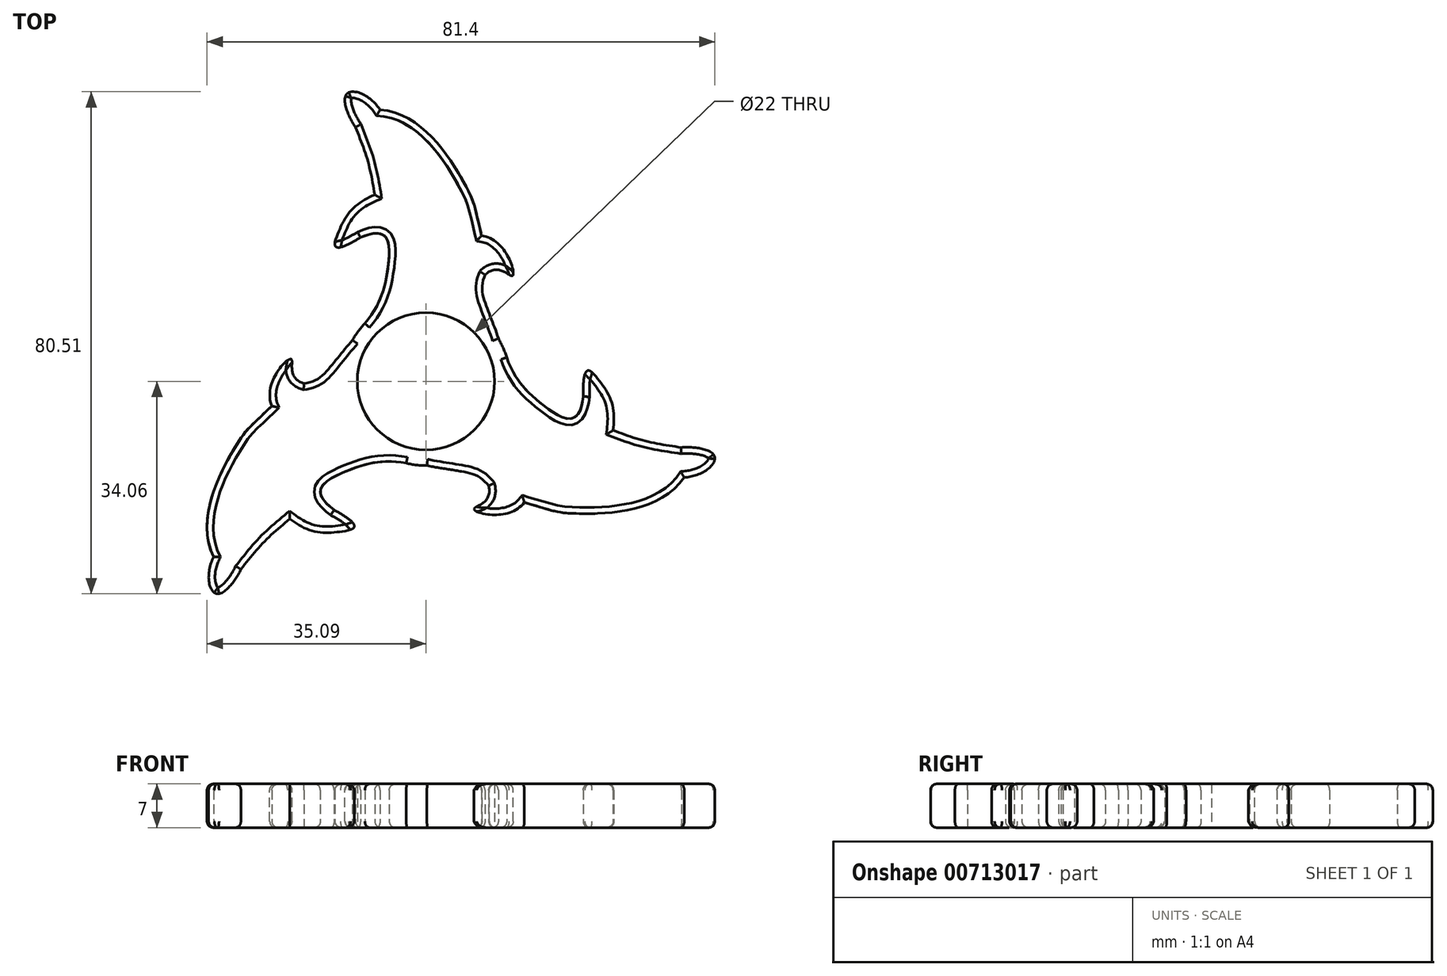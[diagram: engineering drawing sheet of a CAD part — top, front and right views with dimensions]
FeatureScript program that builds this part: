
annotation { "Feature Type Name" : "Feature", "Feature Type Description" : "" }
export const myFeature = defineFeature(function(context is Context, id is Id, definition is map)
    precondition{}
    {
        {
            var Q0;
            Q0=qCreatedBy(makeId("Top.planeOp"),FACE);
            var sketch = newSketch(context, id + "F0", { "sketchPlane" : qUnion([Q0])});
            skCircle(sketch, "E0", {"center": v(0, 0) * mm, "radius": 11 * mm});
            skCircle(sketch, "E1", {"center": v(0, 0) * mm, "radius": 13.5 * mm});
            skFitSpline(sketch, "E2", {"points": [v(-11.28, 40.76) * mm, v(-12.78, 46) * mm, v(-7.35, 43.57) * mm], "startDerivative": vector(-6.4, 8.72) * mm, "endDerivative": vector(10.85, -15.73) * mm});
            skFitSpline(sketch, "E3", {"points": [v(-7.35, 43.57) * mm, v(6.48, 31.13) * mm, v(8.92, 23.38) * mm], "startDerivative": vector(36.08, -2.61) * mm, "endDerivative": vector(9.48, -39.71) * mm});
            skFitSpline(sketch, "E4", {"points": [v(-11.28, 40.76) * mm, v(-9.32, 35.34) * mm, v(-8.2, 29.91) * mm], "startDerivative": vector(4.24, -11.19) * mm, "endDerivative": vector(1.91, -11.06) * mm});
            skFitSpline(sketch, "E5", {"points": [v(8.92, 23.38) * mm, v(13.88, 16.93) * mm, v(9.47, 17.09) * mm], "startDerivative": vector(20.47, -2.87) * mm, "endDerivative": vector(-15.58, -14.46) * mm});
            skFitSpline(sketch, "E6", {"points": [v(9.47, 17.09) * mm, v(9.47, 12.69) * mm, v(11.6, 6.89) * mm], "startDerivative": vector(-4.7, -12.23) * mm, "endDerivative": vector(2.6, -8.41) * mm});
            skFitSpline(sketch, "E7", {"points": [v(-8.2, 29.91) * mm, v(-14.11, 23.7) * mm, v(-10.5, 23.06) * mm], "startDerivative": vector(-19.28, -8.05) * mm, "endDerivative": vector(38.18, 23.27) * mm});
            skFitSpline(sketch, "E8", {"points": [v(-10.5, 23.06) * mm, v(-6.01, 18.9) * mm, v(-9.79, 9.3) * mm], "startDerivative": vector(33.92, 15.13) * mm, "endDerivative": vector(-13.35, -15.48) * mm});
            skLineSegment(sketch, "E9", {"start": v(-59.36, 34.27) * mm, "end": v(57.56, -33.23) * mm, "construction": true});
            skLineSegment(sketch, "E10", {"start": v(-56.64, -32.7) * mm, "end": v(60.28, 34.8) * mm, "construction": true});
            skFitSpline(sketch, "E11.MirrorCS", {"points": [v(-34.05, -28.15) * mm, v(-30.2, -9.95) * mm, v(-24.7, -3.96) * mm], "startDerivative": vector(-15.78, 32.56) * mm, "endDerivative": vector(29.65, 28.07) * mm});
            skFitSpline(sketch, "E12.MirrorCS", {"points": [v(-24.7, -3.96) * mm, v(-21.6, 3.55) * mm, v(-19.54, -0.34) * mm], "startDerivative": vector(-7.75, 19.16) * mm, "endDerivative": vector(20.31, -6.26) * mm});
            skFitSpline(sketch, "E13.MirrorCS", {"points": [v(-19.54, -0.34) * mm, v(-15.72, 1.86) * mm, v(-11.77, 6.6) * mm], "startDerivative": vector(12.94, 2.04) * mm, "endDerivative": vector(5.98, 6.46) * mm});
            skFitSpline(sketch, "E14.MirrorCS", {"points": [v(-14.73, -20.62) * mm, v(-13.36, -14.66) * mm, v(-3.16, -13.12) * mm], "startDerivative": vector(-30.07, 21.8) * mm, "endDerivative": vector(20.08, -3.83) * mm});
            skFitSpline(sketch, "E15.MirrorCS", {"points": [v(-21.8, -22.05) * mm, v(-13.46, -24.07) * mm, v(-14.73, -20.62) * mm], "startDerivative": vector(16.6, -12.67) * mm, "endDerivative": vector(-39.24, 21.43) * mm});
            skFitSpline(sketch, "E16.MirrorCS", {"points": [v(-29.66, -30.15) * mm, v(-25.95, -25.74) * mm, v(-21.8, -22.05) * mm], "startDerivative": vector(7.57, 9.27) * mm, "endDerivative": vector(8.62, 7.19) * mm});
            skFitSpline(sketch, "E17.MirrorCS", {"points": [v(-29.66, -30.15) * mm, v(-33.45, -34.06) * mm, v(-34.05, -28.15) * mm], "startDerivative": vector(-4.35, -9.9) * mm, "endDerivative": vector(8.2, 17.26) * mm});
            skFitSpline(sketch, "E18.MirrorCS", {"points": [v(41.4, -15.41) * mm, v(23.72, -21.18) * mm, v(15.78, -19.42) * mm], "startDerivative": vector(-20.3, -29.94) * mm, "endDerivative": vector(-39.13, 11.64) * mm});
            skFitSpline(sketch, "E19.MirrorCS", {"points": [v(15.78, -19.42) * mm, v(7.72, -20.48) * mm, v(10.06, -16.75) * mm], "startDerivative": vector(-12.72, -16.3) * mm, "endDerivative": vector(-4.74, 20.72) * mm});
            skFitSpline(sketch, "E20.MirrorCS", {"points": [v(10.06, -16.75) * mm, v(6.25, -14.55) * mm, v(0.16, -13.5) * mm], "startDerivative": vector(-8.24, 10.19) * mm, "endDerivative": vector(-8.59, 1.95) * mm});
            skFitSpline(sketch, "E21.MirrorCS", {"points": [v(40.94, -10.61) * mm, v(46.22, -11.93) * mm, v(41.4, -15.41) * mm], "startDerivative": vector(10.74, 1.18) * mm, "endDerivative": vector(-19.04, -1.53) * mm});
            skFitSpline(sketch, "E22.MirrorCS", {"points": [v(40.94, -10.61) * mm, v(35.26, -9.6) * mm, v(30, -7.86) * mm], "startDerivative": vector(-11.81, 1.92) * mm, "endDerivative": vector(-10.54, 3.87) * mm});
            skFitSpline(sketch, "E23.MirrorCS", {"points": [v(30, -7.86) * mm, v(27.57, 0.38) * mm, v(25.22, -2.44) * mm], "startDerivative": vector(2.67, 20.72) * mm, "endDerivative": vector(1.06, -44.7) * mm});
            skFitSpline(sketch, "E24.MirrorCS", {"points": [v(25.22, -2.44) * mm, v(19.37, -4.24) * mm, v(12.95, 3.83) * mm], "startDerivative": vector(-3.85, -36.94) * mm, "endDerivative": vector(-6.73, 19.3) * mm});
            skSolve(sketch);
        }
        {
            var Q0;
            Q0=makeQuery(id+"F0.imprint","IMPRINT",FACE,{"disambiguationData":[TD([[makeQuery(id+"F0.imprint","IMPRINT",EDGE,{"derivedFrom":sQuery(id+"F0.wireOp",EDGE,"E2")}),-1.0]])]});
            var Q1;
            Q1=makeQuery(id+"F0.imprint","IMPRINT",FACE,{"disambiguationData":[TD([[makeQuery(id+"F0.imprint","IMPRINT",EDGE,{"derivedFrom":sQuery(id+"F0.wireOp",EDGE,"E18.MirrorCS")}),-1.0]])]});
            var Q2;
            Q2=makeQuery(id+"F0.imprint","IMPRINT",FACE,{"disambiguationData":[TD([[makeQuery(id+"F0.imprint","IMPRINT",EDGE,{"derivedFrom":sQuery(id+"F0.wireOp",EDGE,"E0")}),-1.0]])]});
            var Q3;
            Q3=makeQuery(id+"F0.imprint","IMPRINT",FACE,{"disambiguationData":[TD([[makeQuery(id+"F0.imprint","IMPRINT",EDGE,{"derivedFrom":sQuery(id+"F0.wireOp",EDGE,"E11.MirrorCS")}),-1.0]])]});
            extrude(context, id + "F1", {"entities" : qUnion([Q0, Q1, Q2, Q3]), "depth" : 7 * mm, "offsetDistance" : 25 * mm});
        }
        {
            var Q0;
            Q0=makeQuery(id+"F1.opExtrude","CAP_EDGE",EDGE,{"disambiguationData":[OSD([sQuery(id+"F0.wireOp",EDGE,"E12.MirrorCS")])],"isStart":false});
            var Q1;
            Q1=makeQuery(id+"F1.opExtrude","CAP_EDGE",EDGE,{"disambiguationData":[OSD([sQuery(id+"F0.wireOp",EDGE,"E5")])],"isStart":false});
            var Q2;
            Q2=makeQuery(id+"F1.opExtrude","CAP_EDGE",EDGE,{"disambiguationData":[OSD([sQuery(id+"F0.wireOp",EDGE,"E3")])],"isStart":false});
            var Q3;
            Q3=makeQuery(id+"F1.opExtrude","CAP_EDGE",EDGE,{"disambiguationData":[OSD([sQuery(id+"F0.wireOp",EDGE,"E2")])],"isStart":false});
            var Q4;
            Q4=makeQuery(id+"F1.opExtrude","CAP_EDGE",EDGE,{"disambiguationData":[OSD([sQuery(id+"F0.wireOp",EDGE,"E4")])],"isStart":false});
            var Q5;
            Q5=makeQuery(id+"F1.opExtrude","CAP_EDGE",EDGE,{"disambiguationData":[OSD([sQuery(id+"F0.wireOp",EDGE,"E7")])],"isStart":false});
            var Q6;
            Q6=makeQuery(id+"F1.opExtrude","CAP_EDGE",EDGE,{"disambiguationData":[OSD([sQuery(id+"F0.wireOp",EDGE,"E8")])],"isStart":false});
            var Q7;
            Q7=makeQuery(id+"F1.opExtrude","CAP_EDGE",EDGE,{"disambiguationData":[OSD([sQuery(id+"F0.wireOp",EDGE,"E13.MirrorCS")])],"isStart":false});
            var Q8;
            {var subQ0=sQuery(id+"F0.wireOp",EDGE,"E1");Q8=makeQuery(id+"F1.opExtrude","CAP_EDGE",EDGE,{"disambiguationData":[OSD([subQ0]),TDD([makeQuery(id+"F0.imprint","IMPRINT",EDGE,{"disambiguationData":[TD([[makeQuery(id+"F0.imprint","INTERSECT",VERTEX,{"derivedFrom":[subQ0,sQuery(id+"F0.wireOp",EDGE,"E8")]}),-1.0]])],"derivedFrom":subQ0})])],"isStart":false});}
            var Q9;
            Q9=makeQuery(id+"F1.opExtrude","CAP_EDGE",EDGE,{"disambiguationData":[OSD([sQuery(id+"F0.wireOp",EDGE,"E11.MirrorCS")])],"isStart":false});
            var Q10;
            Q10=makeQuery(id+"F1.opExtrude","CAP_EDGE",EDGE,{"disambiguationData":[OSD([sQuery(id+"F0.wireOp",EDGE,"E17.MirrorCS")])],"isStart":false});
            var Q11;
            Q11=makeQuery(id+"F1.opExtrude","CAP_EDGE",EDGE,{"disambiguationData":[OSD([sQuery(id+"F0.wireOp",EDGE,"E16.MirrorCS")])],"isStart":false});
            var Q12;
            Q12=makeQuery(id+"F1.opExtrude","CAP_EDGE",EDGE,{"disambiguationData":[OSD([sQuery(id+"F0.wireOp",EDGE,"E15.MirrorCS")])],"isStart":false});
            var Q13;
            Q13=makeQuery(id+"F1.opExtrude","CAP_EDGE",EDGE,{"disambiguationData":[OSD([sQuery(id+"F0.wireOp",EDGE,"E14.MirrorCS")])],"isStart":false});
            var Q14;
            {var subQ0=sQuery(id+"F0.wireOp",EDGE,"E1");Q14=makeQuery(id+"F1.opExtrude","CAP_EDGE",EDGE,{"disambiguationData":[OSD([subQ0]),TDD([makeQuery(id+"F0.imprint","IMPRINT",EDGE,{"disambiguationData":[TD([[makeQuery(id+"F0.imprint","INTERSECT",VERTEX,{"derivedFrom":[subQ0,sQuery(id+"F0.wireOp",EDGE,"E14.MirrorCS")]}),-1.0]])],"derivedFrom":subQ0})])],"isStart":false});}
            var Q15;
            Q15=makeQuery(id+"F1.opExtrude","CAP_EDGE",EDGE,{"disambiguationData":[OSD([sQuery(id+"F0.wireOp",EDGE,"E20.MirrorCS")])],"isStart":false});
            var Q16;
            Q16=makeQuery(id+"F1.opExtrude","CAP_EDGE",EDGE,{"disambiguationData":[OSD([sQuery(id+"F0.wireOp",EDGE,"E19.MirrorCS")])],"isStart":false});
            var Q17;
            Q17=makeQuery(id+"F1.opExtrude","CAP_EDGE",EDGE,{"disambiguationData":[OSD([sQuery(id+"F0.wireOp",EDGE,"E18.MirrorCS")])],"isStart":false});
            var Q18;
            Q18=makeQuery(id+"F1.opExtrude","CAP_EDGE",EDGE,{"disambiguationData":[OSD([sQuery(id+"F0.wireOp",EDGE,"E21.MirrorCS")])],"isStart":false});
            var Q19;
            Q19=makeQuery(id+"F1.opExtrude","CAP_EDGE",EDGE,{"disambiguationData":[OSD([sQuery(id+"F0.wireOp",EDGE,"E22.MirrorCS")])],"isStart":false});
            var Q20;
            Q20=makeQuery(id+"F1.opExtrude","CAP_EDGE",EDGE,{"disambiguationData":[OSD([sQuery(id+"F0.wireOp",EDGE,"E23.MirrorCS")])],"isStart":false});
            var Q21;
            Q21=makeQuery(id+"F1.opExtrude","CAP_EDGE",EDGE,{"disambiguationData":[OSD([sQuery(id+"F0.wireOp",EDGE,"E24.MirrorCS")])],"isStart":false});
            var Q22;
            Q22=makeQuery(id+"F1.opExtrude","CAP_EDGE",EDGE,{"disambiguationData":[OSD([sQuery(id+"F0.wireOp",EDGE,"E6")])],"isStart":false});
            var Q23;
            {var subQ0=sQuery(id+"F0.wireOp",EDGE,"E1");Q23=makeQuery(id+"F1.opExtrude","CAP_EDGE",EDGE,{"disambiguationData":[OSD([subQ0]),TDD([makeQuery(id+"F0.imprint","IMPRINT",EDGE,{"disambiguationData":[TD([[makeQuery(id+"F0.imprint","INTERSECT",VERTEX,{"derivedFrom":[subQ0,sQuery(id+"F0.wireOp",EDGE,"E6")]}),1.0]])],"derivedFrom":subQ0})])],"isStart":false});}
            var Q24;
            Q24=makeQuery(id+"F1.opExtrude","CAP_EDGE",EDGE,{"disambiguationData":[OSD([sQuery(id+"F0.wireOp",EDGE,"E5")])],"isStart":true});
            var Q25;
            Q25=makeQuery(id+"F1.opExtrude","CAP_EDGE",EDGE,{"disambiguationData":[OSD([sQuery(id+"F0.wireOp",EDGE,"E3")])],"isStart":true});
            var Q26;
            Q26=makeQuery(id+"F1.opExtrude","CAP_EDGE",EDGE,{"disambiguationData":[OSD([sQuery(id+"F0.wireOp",EDGE,"E2")])],"isStart":true});
            var Q27;
            Q27=makeQuery(id+"F1.opExtrude","CAP_EDGE",EDGE,{"disambiguationData":[OSD([sQuery(id+"F0.wireOp",EDGE,"E4")])],"isStart":true});
            var Q28;
            Q28=makeQuery(id+"F1.opExtrude","CAP_EDGE",EDGE,{"disambiguationData":[OSD([sQuery(id+"F0.wireOp",EDGE,"E8")])],"isStart":true});
            var Q29;
            Q29=makeQuery(id+"F1.opExtrude","CAP_EDGE",EDGE,{"disambiguationData":[OSD([sQuery(id+"F0.wireOp",EDGE,"E7")])],"isStart":true});
            var Q30;
            Q30=makeQuery(id+"F1.opExtrude","CAP_EDGE",EDGE,{"disambiguationData":[OSD([sQuery(id+"F0.wireOp",EDGE,"E6")])],"isStart":true});
            var Q31;
            {var subQ0=sQuery(id+"F0.wireOp",EDGE,"E1");Q31=makeQuery(id+"F1.opExtrude","CAP_EDGE",EDGE,{"disambiguationData":[OSD([subQ0]),TDD([makeQuery(id+"F0.imprint","IMPRINT",EDGE,{"disambiguationData":[TD([[makeQuery(id+"F0.imprint","INTERSECT",VERTEX,{"derivedFrom":[subQ0,sQuery(id+"F0.wireOp",EDGE,"E6")]}),1.0]])],"derivedFrom":subQ0})])],"isStart":true});}
            var Q32;
            Q32=makeQuery(id+"F1.opExtrude","CAP_EDGE",EDGE,{"disambiguationData":[OSD([sQuery(id+"F0.wireOp",EDGE,"E24.MirrorCS")])],"isStart":true});
            var Q33;
            Q33=makeQuery(id+"F1.opExtrude","CAP_EDGE",EDGE,{"disambiguationData":[OSD([sQuery(id+"F0.wireOp",EDGE,"E23.MirrorCS")])],"isStart":true});
            var Q34;
            Q34=makeQuery(id+"F1.opExtrude","CAP_EDGE",EDGE,{"disambiguationData":[OSD([sQuery(id+"F0.wireOp",EDGE,"E22.MirrorCS")])],"isStart":true});
            var Q35;
            Q35=makeQuery(id+"F1.opExtrude","CAP_EDGE",EDGE,{"disambiguationData":[OSD([sQuery(id+"F0.wireOp",EDGE,"E21.MirrorCS")])],"isStart":true});
            var Q36;
            Q36=makeQuery(id+"F1.opExtrude","CAP_EDGE",EDGE,{"disambiguationData":[OSD([sQuery(id+"F0.wireOp",EDGE,"E18.MirrorCS")])],"isStart":true});
            var Q37;
            Q37=makeQuery(id+"F1.opExtrude","CAP_EDGE",EDGE,{"disambiguationData":[OSD([sQuery(id+"F0.wireOp",EDGE,"E19.MirrorCS")])],"isStart":true});
            var Q38;
            Q38=makeQuery(id+"F1.opExtrude","CAP_EDGE",EDGE,{"disambiguationData":[OSD([sQuery(id+"F0.wireOp",EDGE,"E20.MirrorCS")])],"isStart":true});
            var Q39;
            Q39=makeQuery(id+"F1.opExtrude","CAP_EDGE",EDGE,{"disambiguationData":[OSD([sQuery(id+"F0.wireOp",EDGE,"E14.MirrorCS")])],"isStart":true});
            var Q40;
            {var subQ0=sQuery(id+"F0.wireOp",EDGE,"E1");Q40=makeQuery(id+"F1.opExtrude","CAP_EDGE",EDGE,{"disambiguationData":[OSD([subQ0]),TDD([makeQuery(id+"F0.imprint","IMPRINT",EDGE,{"disambiguationData":[TD([[makeQuery(id+"F0.imprint","INTERSECT",VERTEX,{"derivedFrom":[subQ0,sQuery(id+"F0.wireOp",EDGE,"E14.MirrorCS")]}),-1.0]])],"derivedFrom":subQ0})])],"isStart":true});}
            var Q41;
            Q41=makeQuery(id+"F1.opExtrude","CAP_EDGE",EDGE,{"disambiguationData":[OSD([sQuery(id+"F0.wireOp",EDGE,"E16.MirrorCS")])],"isStart":true});
            var Q42;
            Q42=makeQuery(id+"F1.opExtrude","CAP_EDGE",EDGE,{"disambiguationData":[OSD([sQuery(id+"F0.wireOp",EDGE,"E15.MirrorCS")])],"isStart":true});
            var Q43;
            Q43=makeQuery(id+"F1.opExtrude","CAP_EDGE",EDGE,{"disambiguationData":[OSD([sQuery(id+"F0.wireOp",EDGE,"E17.MirrorCS")])],"isStart":true});
            var Q44;
            Q44=makeQuery(id+"F1.opExtrude","CAP_EDGE",EDGE,{"disambiguationData":[OSD([sQuery(id+"F0.wireOp",EDGE,"E11.MirrorCS")])],"isStart":true});
            var Q45;
            Q45=makeQuery(id+"F1.opExtrude","CAP_EDGE",EDGE,{"disambiguationData":[OSD([sQuery(id+"F0.wireOp",EDGE,"E12.MirrorCS")])],"isStart":true});
            var Q46;
            Q46=makeQuery(id+"F1.opExtrude","CAP_EDGE",EDGE,{"disambiguationData":[OSD([sQuery(id+"F0.wireOp",EDGE,"E13.MirrorCS")])],"isStart":true});
            var Q47;
            {var subQ0=sQuery(id+"F0.wireOp",EDGE,"E1");Q47=makeQuery(id+"F1.opExtrude","CAP_EDGE",EDGE,{"disambiguationData":[OSD([subQ0]),TDD([makeQuery(id+"F0.imprint","IMPRINT",EDGE,{"disambiguationData":[TD([[makeQuery(id+"F0.imprint","INTERSECT",VERTEX,{"derivedFrom":[subQ0,sQuery(id+"F0.wireOp",EDGE,"E8")]}),-1.0]])],"derivedFrom":subQ0})])],"isStart":true});}
            fillet(context, id + "F2", {"entities" : qUnion([Q0, Q1, Q2, Q3, Q4, Q5, Q6, Q7, Q8, Q9, Q10, Q11, Q12, Q13, Q14, Q15, Q16, Q17, Q18, Q19, Q20, Q21, Q22, Q23, Q24, Q25, Q26, Q27, Q28, Q29, Q30, Q31, Q32, Q33, Q34, Q35, Q36, Q37, Q38, Q39, Q40, Q41, Q42, Q43, Q44, Q45, Q46, Q47]), "radius" : 1 * mm, "tangentPropagation" : true, "allowEdgeOverflow" : false});
        }
    });
